# Revit family: Sink-Vessel-Lavatory-KOHLER-Kankara-K-76601IN_1
name_source: partatom
category: Plumbing Fixtures
units: mm (PartAtom-declared; Revit-internal decimal feet)

## family parameters
Cut with Voids When Loaded = No
Host = Face
OmniClass Number = 23.31.13.00
OmniClass Title = Sinks
Part Type = Normal
Room Calculation Point = No
Round Connector Dimension = Use Diameter
Shared = No

## types (5) — shared parameters
ADA Compliant = No
Assembly Code = D2010400
CW Connection = No
Cold Water Inlet = Cold Water Inlet
Date Modified = 02/23/2023
Default Elevation = 36"
Description = Vessel Basin Without Faucet Hole In Black
Drain Included = No
HW Connection = No
Height = 5 1/8"
Hot Water Inlet = Hot Water Inlet
Length = 22 3/16"
Manufacturer = Kohler Co.
Master Format 2014 = 22 41 16
Master Format 2014 Name = Residential Lavatories and Sinks
Material = Vitreous China
Product Documentation Link = https://resources.kohler.com
Product Name = Kankara
URL = https://www.kohler.co.in
Vent Connection = No
Waste Connection = Yes
Waste Water Outlet = Waste Water Outlet
WaterSense Certified = No
Width = 15 7/8"

## per-type parameters (varying)
| type | Finish | Model | Product Page URL | Type |
| 0-White | Kohler-Vitreous_China-0-White | K-76601IN-0 | https://www.kohler.co.in | 1 |
| 7-Black Black | Kohler-Vitreous_China-7-Black_Black | K-76601IN-7 | https://www.kohler.co.in | 2 |
| K4-Cashmere | Kohler-Vitreous_China-K4-Cashmere | K-76601IN-K4 | https://www.kohler.co.in | 3 |
| 47-Almond | Kohler-Vitreous_China-47-Almond | K-76601IN-47 |  | 4 |
| DGS-Indigo | KOHLER-Vitreous_China-DGS-Indigo | K-76601IN-DGS |  | 5 |

## geometry (parser evidence)
native form markers: Sweep x6
no freeform markers — native parametric forms only
